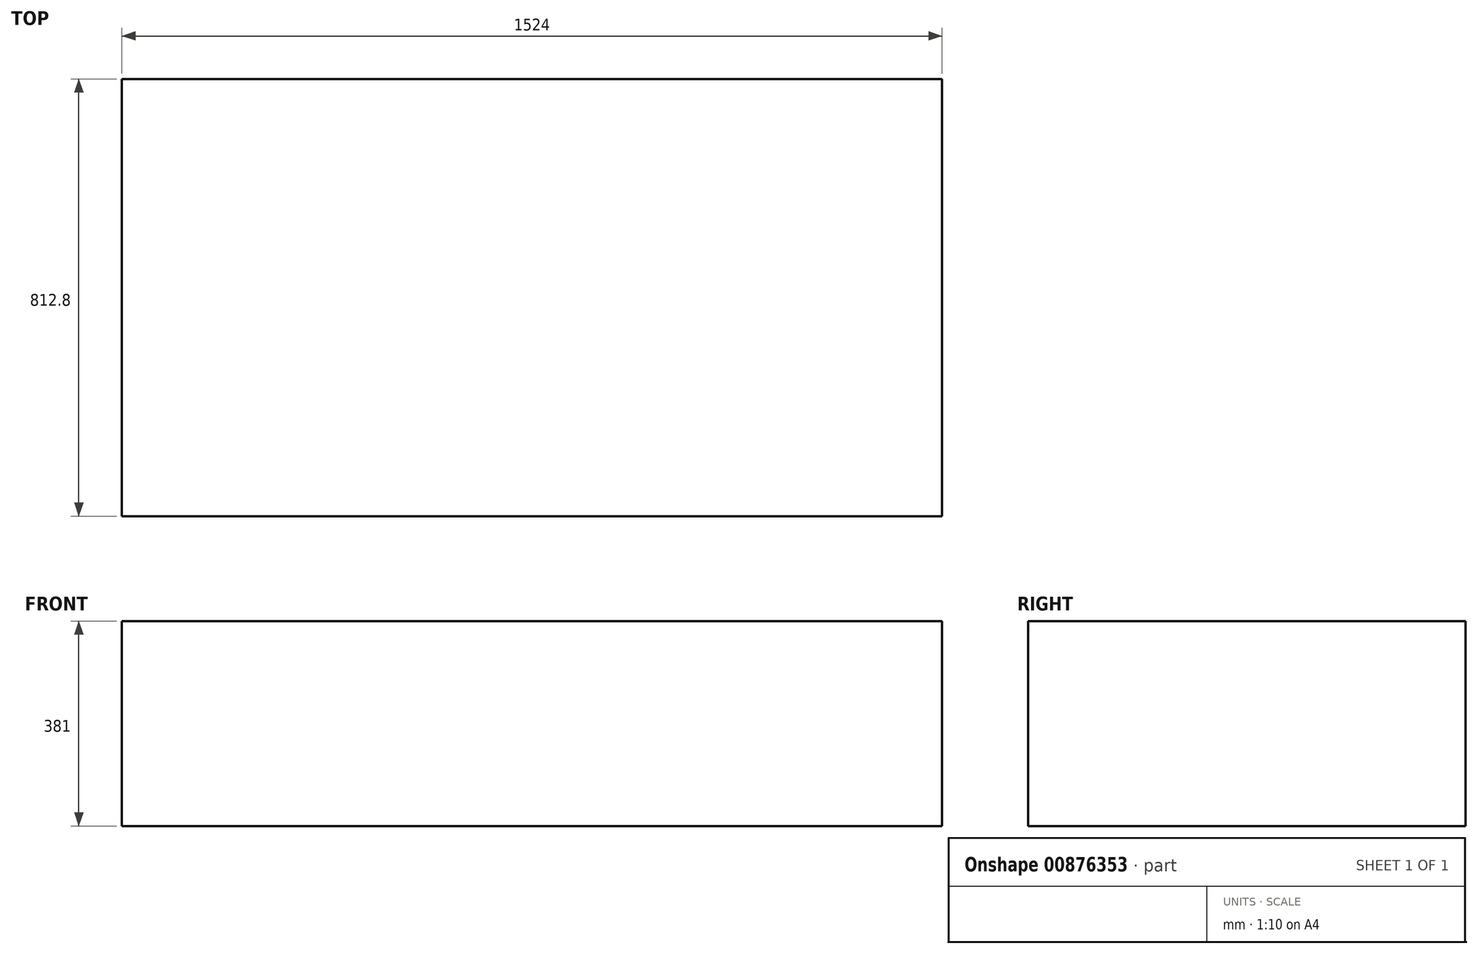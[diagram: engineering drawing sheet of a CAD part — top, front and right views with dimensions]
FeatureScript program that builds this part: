
annotation { "Feature Type Name" : "Feature", "Feature Type Description" : "" }
export const myFeature = defineFeature(function(context is Context, id is Id, definition is map)
    precondition{}
    {
        {
            var Q0;
            Q0=qCreatedBy(makeId("Top.planeOp"),FACE);
            var sketch = newSketch(context, id + "F0", { "sketchPlane" : qUnion([Q0])});
            skLineSegment(sketch, "E0.bottom", {"start": v(762, 406.4) * mm, "end": v(-762, 406.4) * mm});
            skLineSegment(sketch, "E0.top", {"start": v(762, -406.4) * mm, "end": v(-762, -406.4) * mm});
            skLineSegment(sketch, "E0.left", {"start": v(762, 406.4) * mm, "end": v(762, -406.4) * mm});
            skLineSegment(sketch, "E0.right", {"start": v(-762, 406.4) * mm, "end": v(-762, -406.4) * mm});
            skPoint(sketch, "E0.middle", {"position": v(0, 0) * mm});
            skSolve(sketch);
        }
        {
            var Q0;
            Q0=makeQuery(id+"F0.imprint","IMPRINT",FACE,{"disambiguationData":[TD([[makeQuery(id+"F0.imprint","IMPRINT",EDGE,{"derivedFrom":sQuery(id+"F0.wireOp",EDGE,"E0.bottom")}),1.0]])]});
            extrude(context, id + "F1", {"entities" : qUnion([Q0]), "depth" : 381 * mm, "offsetDistance" : 25.4 * mm});
        }
    });
